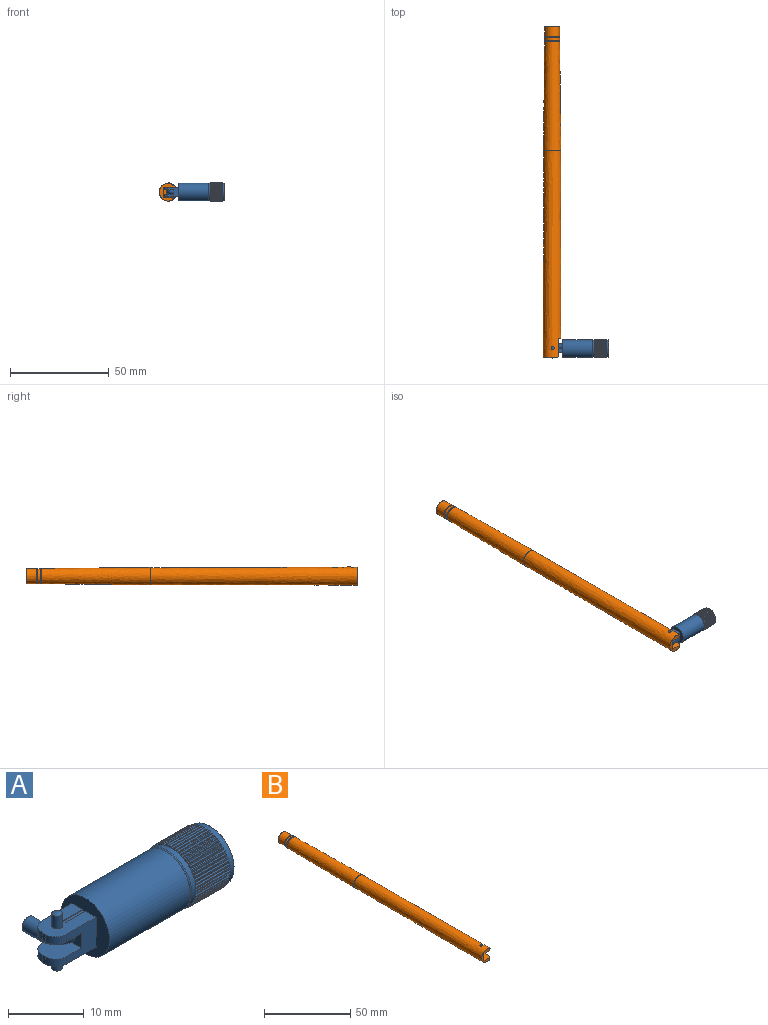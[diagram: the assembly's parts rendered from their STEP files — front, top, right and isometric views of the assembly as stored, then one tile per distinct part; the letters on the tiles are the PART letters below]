
ASSEMBLY  parts=2 mates=1
PART A: 220 faces, bbox 171x79.1x79.2 mm
  f0: plane 9.33x9.33mm, normal (1,0,0), area 3.5mm2, adj f2,f3,f4,f5,f6,f7,f8,f9
  f1: plane 9.33x9.33mm, normal (-1,0,0), area 3.5mm2, adj f2,f3,f4,f5,f6,f7,f8,f9
  f2: revolved ~6.2x2.5mm, area 0.8mm2, adj f0,f1,f209,f211
  f3: torus R=124.96mm, axis (1,0,0), area 1.2mm2, adj f0,f1,f95,f212
  f4: torus R=124.95mm, axis (1,0,0), area 1.2mm2, adj f0,f1,f135,f210
  f5: torus R=124.95mm, axis (1,0,0), area 1.2mm2, adj f0,f1,f206,f207
  f6: torus R=124.96mm, axis (1,0,0), area 1.2mm2, adj f0,f1,f96,f208
  f7: torus R=124.95mm, axis (1,0,0), area 1.2mm2, adj f0,f1,f204,f205
  f8: torus R=124.95mm, axis (1,0,0), area 1.2mm2, adj f0,f1,f202,f203
  f9: torus R=124.95mm, axis (1,0,0), area 1.2mm2, adj f0,f1,f200,f201
  f10: torus R=124.95mm, axis (1,0,0), area 1.2mm2, adj f0,f1,f198,f199
  f11: torus R=124.95mm, axis (1,0,0), area 1.2mm2, adj f0,f1,f196,f197
  f12: torus R=124.95mm, axis (1,0,0), area 1.2mm2, adj f0,f1,f194,f195
  f13: torus R=124.95mm, axis (1,0,0), area 1.2mm2, adj f0,f1,f192,f193
  f14: torus R=124.95mm, axis (1,0,0), area 1.2mm2, adj f0,f1,f190,f191
  f15: torus R=124.95mm, axis (1,0,0), area 1.2mm2, adj f0,f1,f188,f189
  f16: torus R=124.95mm, axis (1,0,0), area 1.2mm2, adj f0,f1,f186,f187
  f17: torus R=124.95mm, axis (1,0,0), area 1.2mm2, adj f0,f1,f184,f185
  f18: torus R=124.95mm, axis (1,0,0), area 1.2mm2, adj f0,f1,f182,f183
  f19: torus R=124.95mm, axis (1,0,0), area 1.2mm2, adj f0,f1,f180,f181
  f20: torus R=124.95mm, axis (1,0,0), area 1.2mm2, adj f0,f1,f178,f179
  f21: torus R=124.95mm, axis (1,0,0), area 1.2mm2, adj f0,f1,f176,f177
  f22: torus R=124.95mm, axis (1,0,0), area 1.2mm2, adj f0,f1,f174,f175
  f23: torus R=124.95mm, axis (1,0,0), area 1.2mm2, adj f0,f1,f172,f173
  f24: torus R=124.95mm, axis (1,0,0), area 1.2mm2, adj f0,f1,f170,f171
  f25: torus R=124.95mm, axis (1,0,0), area 1.2mm2, adj f0,f1,f168,f169
  f26: torus R=124.95mm, axis (1,0,0), area 1.2mm2, adj f0,f1,f166,f167
  f27: torus R=124.95mm, axis (1,0,0), area 1.2mm2, adj f0,f1,f164,f165
  f28: torus R=124.95mm, axis (1,0,0), area 1.2mm2, adj f0,f1,f162,f163
  f29: torus R=124.95mm, axis (1,0,0), area 1.2mm2, adj f0,f1,f160,f161
  f30: torus R=124.95mm, axis (1,0,0), area 1.2mm2, adj f0,f1,f158,f159
  f31: torus R=124.95mm, axis (1,0,0), area 1.2mm2, adj f0,f1,f156,f157
  f32: torus R=124.95mm, axis (1,0,0), area 1.2mm2, adj f0,f1,f154,f155
  f33: torus R=124.95mm, axis (1,0,0), area 1.2mm2, adj f0,f1,f152,f153
  f34: torus R=124.94mm, axis (1,0,0), area 1.2mm2, adj f0,f1,f150,f151
  f35: torus R=124.94mm, axis (1,0,0), area 1.2mm2, adj f0,f1,f98,f149
  f36: torus R=124.95mm, axis (1,0,0), area 1.2mm2, adj f0,f1,f136,f147
  f37: torus R=124.95mm, axis (1,0,0), area 1.2mm2, adj f0,f1,f145,f148
  f38: torus R=124.95mm, axis (1,0,0), area 1.2mm2, adj f0,f1,f143,f146
  f39: torus R=124.95mm, axis (1,0,0), area 1.2mm2, adj f0,f1,f141,f144
  f40: torus R=124.95mm, axis (1,0,0), area 1.2mm2, adj f0,f1,f139,f142
  f41: torus R=124.95mm, axis (1,0,0), area 1.2mm2, adj f0,f1,f137,f140
  f42: torus R=124.95mm, axis (1,0,0), area 1.2mm2, adj f0,f1,f133,f138
  f43: torus R=124.95mm, axis (1,0,0), area 1.2mm2, adj f0,f1,f131,f134
  f44: torus R=124.95mm, axis (1,0,0), area 1.2mm2, adj f0,f1,f129,f132
  f45: torus R=124.95mm, axis (1,0,0), area 1.2mm2, adj f0,f1,f127,f130
  f46: torus R=124.95mm, axis (1,0,0), area 1.2mm2, adj f0,f1,f125,f128
  f47: torus R=124.95mm, axis (1,0,0), area 1.2mm2, adj f0,f1,f123,f126
  f48: torus R=124.95mm, axis (1,0,0), area 1.2mm2, adj f0,f1,f121,f124
  f49: torus R=124.95mm, axis (1,0,0), area 1.2mm2, adj f0,f1,f119,f122
  f50: torus R=124.95mm, axis (1,0,0), area 1.2mm2, adj f0,f1,f117,f120
  f51: torus R=124.95mm, axis (1,0,0), area 1.2mm2, adj f0,f1,f115,f118
  f52: torus R=124.95mm, axis (1,0,0), area 1.2mm2, adj f0,f1,f113,f116
  f53: torus R=124.95mm, axis (1,0,0), area 1.2mm2, adj f0,f1,f111,f114
  f54: torus R=124.95mm, axis (1,0,0), area 1.2mm2, adj f0,f1,f109,f112
  f55: torus R=124.95mm, axis (1,0,0), area 1.2mm2, adj f0,f1,f107,f110
  f56: torus R=124.95mm, axis (1,0,0), area 1.2mm2, adj f0,f1,f105,f108
  f57: torus R=124.95mm, axis (1,0,0), area 1.2mm2, adj f0,f1,f103,f106
  f58: torus R=124.95mm, axis (1,0,0), area 1.2mm2, adj f0,f1,f101,f104
  f59: torus R=124.95mm, axis (1,0,0), area 1.2mm2, adj f0,f1,f99,f102
  f60: torus R=124.94mm, axis (1,0,0), area 1.2mm2, adj f0,f1,f97,f100
  f61: plane 4.51x2.41mm, normal (-1,0,0), area 6.6mm2, adj f63,f64,f85,f86,f87
  f62: plane 1.2x0.5mm, normal (-1,0,0), area 0.6mm2, adj f65,f66,f68,f85
  f63: plane 5.5x4.8mm, normal (0,1,0), area 19.8mm2, adj f61,f65,f67,f68,f71,f83,f85,f86
  f64: plane 5.5x4.8mm, normal (0,-1,0), area 19.8mm2, adj f61,f66,f67,f68,f71,f84,f85,f86
  f65: cylinder r=2mm len=2mm, axis (0,0,1), area 3.8mm2, adj f62,f63,f68,f85
  f66: cylinder r=2mm len=2mm, axis (0,0,-1), area 3.8mm2, adj f62,f64,f68,f85
  f67: plane 7.5x4.5mm, normal (0,0,-1), area 28.6mm2, adj f63,f64,f69,f71,f73,f75,f80,f82
  f68: plane 7.5x4.5mm, normal (0,0,1), area 28.6mm2, adj f62,f63,f64,f65,f66,f71,f77,f78
  f69: plane 1.2x0.5mm, normal (-1,0,0), area 0.6mm2, adj f67,f83,f84,f86
  f70: cylinder r=4.5mm len=15mm, axis (1,0,0), area 424.1mm2, adj f71,f72
  f71: plane 9x9mm, normal (-1,0,0), area 42.1mm2, adj f63,f64,f67,f68,f70,f73,f74,f75
  f72: plane 9x9mm, normal (1,0,0), area 10.8mm2, adj f70,f89
  f73: plane 3.75x0.1mm, normal (0,1,0), area 0.4mm2, adj f67,f71,f74,f80
  f74: plane 3.75x0.5mm, normal (0,0,-1), area 1.9mm2, adj f71,f73,f75,f80
  f75: plane 3.75x0.1mm, normal (0,-1,0), area 0.4mm2, adj f67,f71,f74,f80
  f76: plane 3.75x0.5mm, normal (0,0,1), area 1.9mm2, adj f71,f77,f78,f79
  f77: plane 3.75x0.1mm, normal (0,1,0), area 0.4mm2, adj f68,f71,f76,f79
  f78: plane 3.75x0.1mm, normal (0,-1,0), area 0.4mm2, adj f68,f71,f76,f79
  f79: plane 0.5x0.1mm, normal (1,0,0), area 0.1mm2, adj f68,f76,f77,f78
  f80: plane 0.5x0.1mm, normal (1,0,0), area 0mm2, adj f67,f73,f74,f75
  f81: cylinder r=0.7mm len=2mm, axis (0,0,-1), area 8.8mm2, adj f68,f217
  f82: cylinder r=0.7mm len=2mm, axis (0,0,1), area 8.8mm2, adj f67,f218
  f83: cylinder r=2mm len=2mm, axis (0,0,1), area 3.8mm2, adj f63,f67,f69,f86
  f84: cylinder r=2mm len=2mm, axis (0,0,-1), area 3.8mm2, adj f64,f67,f69,f86
  f85: plane 4.75x4.5mm, normal (0,0,-1), area 19.7mm2, adj f61,f62,f63,f64,f65,f66
  f86: plane 4.75x4.5mm, normal (0,0,1), area 19.7mm2, adj f61,f63,f64,f69,f83,f84
  f87: torus R=2.5mm, axis (0,0,1), area 26.6mm2, adj f61,f88
  f88: cylinder r=1.15mm len=2.9mm, axis (0,1,0), area 21mm2, adj f87,f219
  f89: cylinder r=4.1mm len=8.2mm, axis (1,0,0), area 2.6mm2, adj f72,f90
  f90: plane 8.57x8.57mm, normal (-1,0,0), area 4.9mm2, adj f89,f92
  f91: cylinder r=4.49mm len=8.97mm, axis (1,0,0), area 22.6mm2, adj f1,f92
  f92: torus R=4.29mm, axis (-1,0,0), area 8.7mm2, adj f90,f91
  f93: plane 8.77x8.77mm, normal (1,0,0), area 20mm2, adj f213,f216
  f94: cylinder r=4.49mm len=8.97mm, axis (1,0,0), area 25.4mm2, adj f0,f213
  f95: plane 6.2x0.2mm, normal (0,0.56,0.83), area 1.2mm2, adj f0,f1,f3,f96
  f96: plane 6.2x0.22mm, normal (0,0.94,-0.33), area 1.2mm2, adj f0,f1,f6,f95
  f97: plane 6.2x0.23mm, normal (0,-0.98,0.18), area 1.2mm2, adj f0,f1,f60,f98
  f98: plane 6.2x0.22mm, normal (0,-0.42,-0.91), area 1.2mm2, adj f0,f1,f35,f97
  f99: plane 6.2x0.23mm, normal (0,-1,0.07), area 1.2mm2, adj f0,f1,f59,f100
  f100: plane 6.2x0.22mm, normal (0,-0.32,-0.95), area 1.2mm2, adj f0,f1,f60,f99
  f101: plane 6.2x0.23mm, normal (0,-1,-0.03), area 1.2mm2, adj f0,f1,f58,f102
  f102: plane 6.2x0.23mm, normal (0,-0.22,-0.98), area 1.2mm2, adj f0,f1,f59,f101
  f103: plane 6.2x0.23mm, normal (0,-0.99,-0.14), area 1.2mm2, adj f0,f1,f57,f104
  f104: plane 6.2x0.24mm, normal (0,-0.11,-0.99), area 1.2mm2, adj f0,f1,f58,f103
  f105: plane 6.2x0.23mm, normal (0,-0.97,-0.25), area 1.2mm2, adj f0,f1,f56,f106
  f106: plane 6.2x0.24mm, normal (0,-0.01,-1), area 1.2mm2, adj f0,f1,f57,f105
  f107: plane 6.2x0.22mm, normal (0,-0.94,-0.35), area 1.2mm2, adj f0,f1,f55,f108
  f108: plane 6.2x0.24mm, normal (0,0.1,-1), area 1.2mm2, adj f0,f1,f56,f107
  f109: plane 6.2x0.21mm, normal (0,-0.9,-0.44), area 1.2mm2, adj f0,f1,f54,f110
  f110: plane 6.2x0.23mm, normal (0,0.2,-0.98), area 1.2mm2, adj f0,f1,f55,f109
  f111: plane 6.2x0.2mm, normal (0,-0.84,-0.54), area 1.2mm2, adj f0,f1,f53,f112
  f112: plane 6.2x0.23mm, normal (0,0.31,-0.95), area 1.2mm2, adj f0,f1,f54,f111
  f113: plane 6.2x0.18mm, normal (0,-0.78,-0.62), area 1.2mm2, adj f0,f1,f52,f114
  f114: plane 6.2x0.22mm, normal (0,0.41,-0.91), area 1.2mm2, adj f0,f1,f53,f113
  f115: plane 6.2x0.17mm, normal (0,-0.71,-0.7), area 1.2mm2, adj f0,f1,f51,f116
  f116: plane 6.2x0.21mm, normal (0,0.5,-0.87), area 1.2mm2, adj f0,f1,f52,f115
  f117: plane 6.2x0.18mm, normal (0,-0.63,-0.78), area 1.2mm2, adj f0,f1,f50,f118
  f118: plane 6.2x0.19mm, normal (0,0.59,-0.81), area 1.2mm2, adj f0,f1,f51,f117
  f119: plane 6.2x0.2mm, normal (0,-0.55,-0.84), area 1.2mm2, adj f0,f1,f49,f120
  f120: plane 6.2x0.18mm, normal (0,0.67,-0.74), area 1.2mm2, adj f0,f1,f50,f119
  f121: plane 6.2x0.21mm, normal (0,-0.45,-0.89), area 1.2mm2, adj f0,f1,f48,f122
  f122: plane 6.2x0.18mm, normal (0,0.75,-0.66), area 1.2mm2, adj f0,f1,f49,f121
  f123: plane 6.2x0.22mm, normal (0,-0.36,-0.93), area 1.2mm2, adj f0,f1,f47,f124
  f124: plane 6.2x0.19mm, normal (0,0.81,-0.58), area 1.2mm2, adj f0,f1,f48,f123
  f125: plane 6.2x0.23mm, normal (0,-0.26,-0.97), area 1.2mm2, adj f0,f1,f46,f126
  f126: plane 6.2x0.21mm, normal (0,0.87,-0.49), area 1.2mm2, adj f0,f1,f47,f125
  f127: plane 6.2x0.23mm, normal (0,-0.15,-0.99), area 1.2mm2, adj f0,f1,f45,f128
  f128: plane 6.2x0.22mm, normal (0,0.92,-0.4), area 1.2mm2, adj f0,f1,f46,f127
  f129: plane 6.2x0.23mm, normal (0,-0.05,-1), area 1.2mm2, adj f0,f1,f44,f130
  f130: plane 6.2x0.23mm, normal (0,0.96,-0.3), area 1.2mm2, adj f0,f1,f45,f129
  f131: plane 6.2x0.23mm, normal (0,0.06,-1), area 1.2mm2, adj f0,f1,f43,f132
  f132: plane 6.2x0.23mm, normal (0,0.98,-0.19), area 1.2mm2, adj f0,f1,f44,f131
  f133: plane 6.2x0.23mm, normal (0,0.17,-0.99), area 1.2mm2, adj f0,f1,f42,f134
  f134: plane 6.2x0.24mm, normal (0,1,-0.09), area 1.2mm2, adj f0,f1,f43,f133
  f135: plane 6.2x0.19mm, normal (0,0.79,-0.61), area 1.2mm2, adj f0,f1,f4,f136
  f136: plane 6.2x0.19mm, normal (0,0.79,0.61), area 1.2mm2, adj f0,f1,f36,f135
  f137: plane 6.2x0.23mm, normal (0,0.27,-0.96), area 1.2mm2, adj f0,f1,f41,f138
  f138: plane 6.2x0.24mm, normal (0,1,0.02), area 1.2mm2, adj f0,f1,f42,f137
  f139: plane 6.2x0.22mm, normal (0,0.37,-0.93), area 1.2mm2, adj f0,f1,f40,f140
  f140: plane 6.2x0.24mm, normal (0,0.99,0.12), area 1.2mm2, adj f0,f1,f41,f139
  f141: plane 6.2x0.21mm, normal (0,0.47,-0.88), area 1.2mm2, adj f0,f1,f39,f142
  f142: plane 6.2x0.23mm, normal (0,0.97,0.23), area 1.2mm2, adj f0,f1,f40,f141
  f143: plane 6.2x0.19mm, normal (0,0.56,-0.83), area 1.2mm2, adj f0,f1,f38,f144
  f144: plane 6.2x0.22mm, normal (0,0.94,0.33), area 1.2mm2, adj f0,f1,f39,f143
  f145: plane 6.2x0.18mm, normal (0,0.64,-0.76), area 1.2mm2, adj f0,f1,f37,f146
  f146: plane 6.2x0.21mm, normal (0,0.9,0.43), area 1.2mm2, adj f0,f1,f38,f145
  f147: plane 6.2x0.17mm, normal (0,0.72,-0.69), area 1.2mm2, adj f0,f1,f36,f148
  f148: plane 6.2x0.2mm, normal (0,0.85,0.52), area 1.2mm2, adj f0,f1,f37,f147
  f149: plane 6.2x0.22mm, normal (0,-0.96,0.28), area 1.2mm2, adj f0,f1,f35,f150
  f150: plane 6.2x0.2mm, normal (0,-0.51,-0.86), area 1.2mm2, adj f0,f1,f34,f149
  f151: plane 6.2x0.22mm, normal (0,-0.92,0.38), area 1.2mm2, adj f0,f1,f34,f152
  f152: plane 6.2x0.19mm, normal (0,-0.6,-0.8), area 1.2mm2, adj f0,f1,f33,f151
  f153: plane 6.2x0.21mm, normal (0,-0.88,0.48), area 1.2mm2, adj f0,f1,f33,f154
  f154: plane 6.2x0.17mm, normal (0,-0.68,-0.73), area 1.2mm2, adj f0,f1,f32,f153
  f155: plane 6.2x0.19mm, normal (0,-0.82,0.57), area 1.2mm2, adj f0,f1,f32,f156
  f156: plane 6.2x0.18mm, normal (0,-0.76,-0.65), area 1.2mm2, adj f0,f1,f31,f155
  f157: plane 6.2x0.18mm, normal (0,-0.76,0.65), area 1.2mm2, adj f0,f1,f31,f158
  f158: plane 6.2x0.2mm, normal (0,-0.82,-0.57), area 1.2mm2, adj f0,f1,f30,f157
  f159: plane 6.2x0.17mm, normal (0,-0.68,0.73), area 1.2mm2, adj f0,f1,f30,f160
  f160: plane 6.2x0.21mm, normal (0,-0.88,-0.48), area 1.2mm2, adj f0,f1,f29,f159
  f161: plane 6.2x0.19mm, normal (0,-0.6,0.8), area 1.2mm2, adj f0,f1,f29,f162
  f162: plane 6.2x0.22mm, normal (0,-0.92,-0.38), area 1.2mm2, adj f0,f1,f28,f161
  f163: plane 6.2x0.2mm, normal (0,-0.51,0.86), area 1.2mm2, adj f0,f1,f28,f164
  f164: plane 6.2x0.23mm, normal (0,-0.96,-0.28), area 1.2mm2, adj f0,f1,f27,f163
  f165: plane 6.2x0.21mm, normal (0,-0.42,0.91), area 1.2mm2, adj f0,f1,f27,f166
  f166: plane 6.2x0.23mm, normal (0,-0.98,-0.18), area 1.2mm2, adj f0,f1,f26,f165
  f167: plane 6.2x0.22mm, normal (0,-0.32,0.95), area 1.2mm2, adj f0,f1,f26,f168
  f168: plane 6.2x0.24mm, normal (0,-1,-0.07), area 1.2mm2, adj f0,f1,f25,f167
  f169: plane 6.2x0.23mm, normal (0,-0.22,0.98), area 1.2mm2, adj f0,f1,f25,f170
  f170: plane 6.2x0.24mm, normal (0,-1,0.03), area 1.2mm2, adj f0,f1,f24,f169
  f171: plane 6.2x0.23mm, normal (0,-0.11,0.99), area 1.2mm2, adj f0,f1,f24,f172
  f172: plane 6.2x0.23mm, normal (0,-0.99,0.14), area 1.2mm2, adj f0,f1,f23,f171
  f173: plane 6.2x0.23mm, normal (0,-0.01,1), area 1.2mm2, adj f0,f1,f23,f174
  f174: plane 6.2x0.23mm, normal (0,-0.97,0.25), area 1.2mm2, adj f0,f1,f22,f173
  f175: plane 6.2x0.23mm, normal (0,0.1,1), area 1.2mm2, adj f0,f1,f22,f176
  f176: plane 6.2x0.22mm, normal (0,-0.94,0.35), area 1.2mm2, adj f0,f1,f21,f175
  f177: plane 6.2x0.23mm, normal (0,0.2,0.98), area 1.2mm2, adj f0,f1,f21,f178
  f178: plane 6.2x0.21mm, normal (0,-0.9,0.44), area 1.2mm2, adj f0,f1,f20,f177
  f179: plane 6.2x0.22mm, normal (0,0.31,0.95), area 1.2mm2, adj f0,f1,f20,f180
  f180: plane 6.2x0.2mm, normal (0,-0.84,0.54), area 1.2mm2, adj f0,f1,f19,f179
  f181: plane 6.2x0.21mm, normal (0,0.41,0.91), area 1.2mm2, adj f0,f1,f19,f182
  f182: plane 6.2x0.19mm, normal (0,-0.78,0.62), area 1.2mm2, adj f0,f1,f18,f181
  f183: plane 6.2x0.2mm, normal (0,0.5,0.87), area 1.2mm2, adj f0,f1,f18,f184
  f184: plane 6.2x0.17mm, normal (0,-0.71,0.7), area 1.2mm2, adj f0,f1,f17,f183
  f185: plane 6.2x0.19mm, normal (0,0.59,0.81), area 1.2mm2, adj f0,f1,f17,f186
  f186: plane 6.2x0.18mm, normal (0,-0.63,0.78), area 1.2mm2, adj f0,f1,f16,f185
  f187: plane 6.2x0.17mm, normal (0,0.67,0.74), area 1.2mm2, adj f0,f1,f16,f188
  f188: plane 6.2x0.2mm, normal (0,-0.55,0.84), area 1.2mm2, adj f0,f1,f15,f187
  f189: plane 6.2x0.18mm, normal (0,0.75,0.66), area 1.2mm2, adj f0,f1,f15,f190
  f190: plane 6.2x0.21mm, normal (0,-0.45,0.89), area 1.2mm2, adj f0,f1,f14,f189
  f191: plane 6.2x0.19mm, normal (0,0.81,0.58), area 1.2mm2, adj f0,f1,f14,f192
  f192: plane 6.2x0.22mm, normal (0,-0.36,0.93), area 1.2mm2, adj f0,f1,f13,f191
  f193: plane 6.2x0.2mm, normal (0,0.87,0.49), area 1.2mm2, adj f0,f1,f13,f194
  f194: plane 6.2x0.23mm, normal (0,-0.26,0.97), area 1.2mm2, adj f0,f1,f12,f193
  f195: plane 6.2x0.22mm, normal (0,0.92,0.4), area 1.2mm2, adj f0,f1,f12,f196
  f196: plane 6.2x0.23mm, normal (0,-0.15,0.99), area 1.2mm2, adj f0,f1,f11,f195
  f197: plane 6.2x0.22mm, normal (0,0.96,0.3), area 1.2mm2, adj f0,f1,f11,f198
  f198: plane 6.2x0.24mm, normal (0,-0.05,1), area 1.2mm2, adj f0,f1,f10,f197
  f199: plane 6.2x0.23mm, normal (0,0.98,0.19), area 1.2mm2, adj f0,f1,f10,f200
  f200: plane 6.2x0.24mm, normal (0,0.06,1), area 1.2mm2, adj f0,f1,f9,f199
  f201: plane 6.2x0.23mm, normal (0,1,0.09), area 1.2mm2, adj f0,f1,f9,f202
  f202: plane 6.2x0.23mm, normal (0,0.17,0.99), area 1.2mm2, adj f0,f1,f8,f201
  f203: plane 6.2x0.23mm, normal (0,1,-0.02), area 1.2mm2, adj f0,f1,f8,f204
  f204: plane 6.2x0.23mm, normal (0,0.27,0.96), area 1.2mm2, adj f0,f1,f7,f203
  f205: plane 6.2x0.23mm, normal (0,0.99,-0.12), area 1.2mm2, adj f0,f1,f7,f206
  f206: plane 6.2x0.22mm, normal (0,0.37,0.93), area 1.2mm2, adj f0,f1,f5,f205
  f207: plane 6.2x0.23mm, normal (0,0.97,-0.23), area 1.2mm2, adj f0,f1,f5,f208
  f208: plane 6.2x0.21mm, normal (0,0.47,0.88), area 1.2mm2, adj f0,f1,f6,f207
  f209: plane 6.3x0.3mm, normal (0,0.85,-0.52), area 1.2mm2, adj f0,f1,f2,f210
  f210: plane 6.2x0.17mm, normal (0,0.72,0.69), area 1.2mm2, adj f0,f1,f4,f209
  f211: plane 6.3x0.28mm, normal (0,0.64,0.76), area 1.2mm2, adj f0,f1,f2,f212
  f212: plane 6.2x0.21mm, normal (0,0.9,-0.43), area 1.2mm2, adj f0,f1,f3,f211
  f213: cone r=4.39mm half-angle=45deg, axis (-1,0,0), area 3.9mm2, adj f93,f94
  f214: cylinder r=3.49mm len=6.97mm, axis (1,0,0), area 129.3mm2, adj f215,f216
  f215: plane 6.97x6.97mm, normal (1,0,0), area 38.2mm2, adj f214
  f216: cone r=3.49mm half-angle=45deg, axis (1,0,0), area 3.1mm2, adj f93,f214
  f217: bspline ~1.49x1.43mm, area 1.7mm2, adj f81
  f218: bspline ~1.49x1.43mm, area 1.7mm2, adj f82
  f219: plane 2.3x2.3mm, normal (0,1,0), area 4.2mm2, adj f88
PART B: 23 faces, bbox 9.1x168.2x9.1 mm
  f0: bspline ~7.67x7.67mm, area 36mm2, adj f1,f2
  f1: plane 7.72x7.72mm, normal (0,-1,0), area 8.5mm2, adj f0,f3
  f2: plane 7.69x7.69mm, normal (0,1,0), area 9.5mm2, adj f0,f4
  f3: cylinder r=3.46mm len=6.92mm, axis (0,1,0), area 10.9mm2, adj f1,f5
  f4: cylinder r=3.4mm len=6.79mm, axis (0,1,0), area 10.7mm2, adj f2,f6
  f5: plane 7.73x7.73mm, normal (0,1,0), area 8.7mm2, adj f3,f7
  f6: plane 7.68x7.68mm, normal (0,-1,0), area 9.4mm2, adj f4,f8
  f7: bspline ~60.5x8.86mm, area 1429.1mm2, adj f5,f9
  f8: bspline ~7.63x7.63mm, area 130.7mm2, adj f6,f10
  f9: plane 8.97x8.97mm, normal (0,-1,0), area 3.8mm2, adj f7,f11
  f10: sphere r=3.75mm, area 85.2mm2, adj f8
  f11: bspline ~105x9mm, area 2824.9mm2, adj f9,f12,f13,f14,f15,f16,f17,f18
  f12: cylinder r=1mm len=1.48mm, axis (0,0,1), area 1.7mm2, adj f11,f13,f17,f20
  f13: plane 9x0.75mm, normal (1,0,0), area 6.7mm2, adj f11,f12,f14,f20
  f14: plane 7.06x6.53mm, normal (0,-1,0), area 34.2mm2, adj f11,f13,f15,f20,f21,f22
  f15: plane 9x0.75mm, normal (1,0,0), area 6.7mm2, adj f11,f14,f16,f22
  f16: cylinder r=1mm len=1.48mm, axis (0,0,1), area 1.7mm2, adj f11,f15,f17,f22
  f17: plane 9.1x6.71mm, normal (0,-1,0), area 27.1mm2, adj f11,f12,f16,f20,f21,f22
  f18: cylinder r=0.75mm len=1.99mm, axis (0,0,1), area 9.4mm2, adj f11,f20
  f19: cylinder r=0.75mm len=1.86mm, axis (0,0,1), area 8.7mm2, adj f11,f22
  f20: plane 10x5.61mm, normal (0,0,-1), area 54.1mm2, adj f12,f13,f14,f17,f18,f21
  f21: plane 10x5mm, normal (1,0,0), area 50mm2, adj f14,f17,f20,f22
  f22: plane 10x5.61mm, normal (0,0,1), area 54.1mm2, adj f14,f15,f16,f17,f19,f21
PLACE A t=(-23.64,-4.76,-0.03)mm fixed
PLACE B t=(-23.64,-4.75,-0.1)mm
MATE revolute A.f82 <-> B.f18  axis (0,0,1) through (-23.3,0.25,2.4)mm
